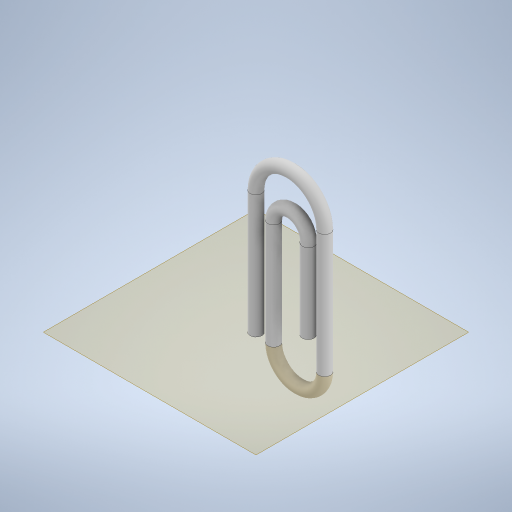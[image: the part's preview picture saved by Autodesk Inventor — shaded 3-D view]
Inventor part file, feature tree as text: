
AUTODESK INVENTOR PART (.ipt)
format: ipt  version: 2024 (Build 280153000, 153)  size: 284,672 bytes
history: native  units: in
note: dims shown in document units (in); Inventor stores cm internally (conversion verified against a paired STEP export)
features: sketch x2, plane x1, sweep x1
ambient origin geometry x8: Origin, YZ Plane, XZ Plane, XY Plane, X Axis, Y Axis, Z Axis, Center Point
bodies: Solid1 (feature_tree)
feature tree (4):
  sketch  "Sketch1"  dims[d0=0.0in d1=0.0in]
  plane  "Work Plane1"
  sweep  "Sweep1"
  sketch  "Sketch2"
